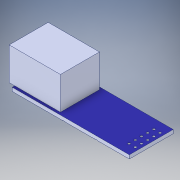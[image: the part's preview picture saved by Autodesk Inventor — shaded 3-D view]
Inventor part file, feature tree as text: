
AUTODESK INVENTOR PART (.ipt)
format: ipt  version: 2018 (Build 220112000, 112)  size: 229,888 bytes
history: native  units: in
note: dims shown in document units (in); Inventor stores cm internally (conversion verified against a paired STEP export)
features: extrude x2, other x2, sketch x1, hole x1
ambient origin geometry x8: Origin, YZ Plane, XZ Plane, XY Plane, X Axis, Y Axis, Z Axis, Center Point
bodies: Solid1 (feature_tree), Solid2 (feature_tree), Solid16 (feature_tree)
feature tree (6):
  sketch  "Sketch1"  dims[d0=0.7087in d1=0.0394in d2=1.8898in d3=0.3937in d4=0.0in d5=0.037in d6=0.7874in d8=0.1in d9=1.9685in d11=0.1in d14=0.3543in d15=0.0591in d16=0.3937in d17=0.0in]
  extrude  "Extrusion1"  Depth=0.0394in
  extrude  "Extrusion2"  Depth=1.8898in
  other  "Housing"
  hole  "Hole"  [1 undecoded]
  other  "PCB"
note: 1 required parameter value undecoded (feature->parameter linkage not recoverable at this tier; creation-order binding heuristic only, values carry confidence <= 0.55)
